# Revit family: Bath-Alcove-KOHLER-Bellwether-K-838
name_source: partatom
category: Plumbing Fixtures
units: mm (PartAtom-declared; Revit-internal decimal feet)

## family parameters
Cut with Voids When Loaded = No
Host = Face
OmniClass Number = 23.31.15.00
Part Type = Normal
Room Calculation Point = No
Round Connector Dimension = Use Diameter
Shared = No

## types (5) — shared parameters
ADA Compliant = Yes
Assembly Code = D2010500
CW Connection = No
Cold Water Inlet = Cold Water Inlet
Date Modified = 11/2/2023
Default Elevation = 0"
Description = 60 Inch x 30-1/4 Inch Alcove Bath, Right Drain
Drain Included = No
HW Connection = No
Height = 14 1/2"
Hot Water Inlet = Hot Water Inlet
Length = 60"
Manufacturer = Kohler Co.
Master Format 2014 = 22 41 19
Master Format 2014 Name = Residential Bathtubs
Material = Enameled Cast Iron
Product Documentation Link = https://www.us.kohler.com
Product Name = Bellwether
Product Page URL = http://www.us.kohler.com
URL = https://www.us.kohler.com
Vent Connection = No
Waste Connection = Yes
Waste Water Outlet = Waste Water Outlet
WaterSense Certified = No
Width = 30 1/4"

## per-type parameters (varying)
| type | Finish | Model | Type |
| 0-White | KOHLER-Enameled_Cast_Iron-0-White | K-838-0 | 1 |
| 17-Teal | KOHLER-Enameled_Cast_Iron-17-Teal | K-838-17 | 2 |
| 34-Fresh Green | KOHLER-Enameled_Cast_Iron-34-Fresh_Green | K-838-34 | 3 |
| 42-Aspen Green | KOHLER-Enameled_Cast_Iron-42-Aspen_Green | K-838-42 | 4 |
| 96-Biscuit | KOHLER-Enameled_Cast_Iron-96-Biscuit | K-838-96 | 5 |

## geometry (parser evidence)
native form markers: Sweep x4
no freeform markers — native parametric forms only
